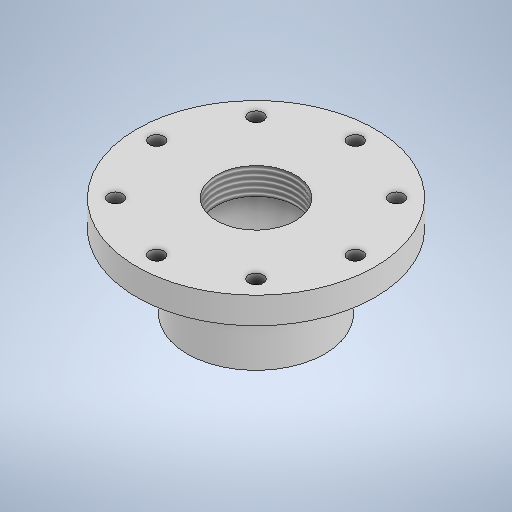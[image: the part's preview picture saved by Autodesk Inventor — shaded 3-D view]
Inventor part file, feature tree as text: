
AUTODESK INVENTOR PART (.ipt)
format: ipt  version: 2025 (Build 290162000, 162)  size: 297,984 bytes
history: native  units: in
note: dims shown in document units (in); Inventor stores cm internally (conversion verified against a paired STEP export)
features: sketch x7, extrude x4, hole x2
ambient origin geometry x8: Origin, YZ Plane, XZ Plane, XY Plane, X Axis, Y Axis, Z Axis, Center Point
bodies: Solid1 (feature_tree)
feature tree (13):
  extrude  "Extrusion1"  Depth=0.3937in TaperAngle=0.0deg
  extrude  "Extrusion2"  Depth=1.1024in TaperAngle=0.0deg
  extrude  "Extrusion3"  Depth=1.1024in TaperAngle=0.0deg
  extrude  "Extrusion4"  Depth=1.9528in
  hole  "Hole1"  [1 undecoded]
  hole  "Hole2"  [1 undecoded]
  sketch  "Sketch1"  dims[d0=3.5433in d1=0.3937in d2=0.0in]
  sketch  "Sketch2"  dims[d6=1.6535in d7=1.1024in d8=0.0in]
  sketch  "Sketch3"  dims[d9=1.7402in d10=1.9528in]
  sketch  "Sketch4"  dims[d11=0.0866in d12=0.0in]
  sketch  "Sketch5"  dims[d13=1.1746in d14=2.5197in d15=0.1575in d16=0.0787in d17=90.0deg d18=2.3346in d19=0.8108in d20=1.4764in]
  sketch  "Sketch6"  dims[d21=0.2165in d22=0.3937in d23=0.4094in d24=0.0787in d25=90.0deg d26=0.315in d27=0.8108in d28=3.1496in d30=360.0deg]
  sketch  "Sketch Circular Pattern1"  dims[d3=2.0472in d4=1.1024in d5=0.0in]
note: 2 required parameter values undecoded (feature->parameter linkage not recoverable at this tier; creation-order binding heuristic only, values carry confidence <= 0.55)
